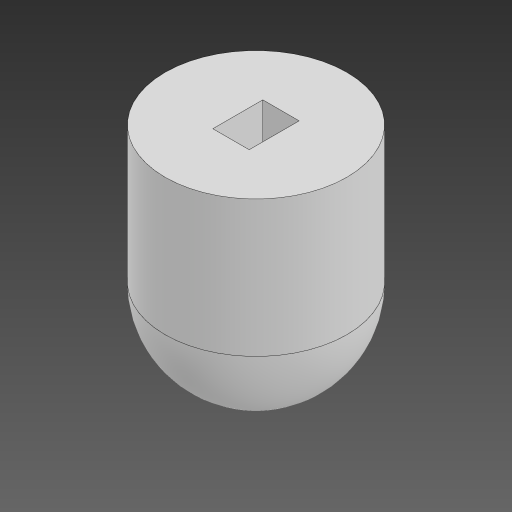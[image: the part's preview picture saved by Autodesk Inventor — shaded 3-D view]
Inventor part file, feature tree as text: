
AUTODESK INVENTOR PART (.ipt)
format: ipt  version: 2023.2 (Build 272271000, 271)  size: 117,248 bytes
history: native  units: mm
features: extrude x2, sketch x1, fillet x1
ambient origin geometry x8: Origin, YZ Plane, XZ Plane, XY Plane, X Axis, Y Axis, Z Axis, Center Point
bodies: Solid1 (feature_tree)
feature tree (4):
  sketch  "Sketch1"  dims[d0=1.6mm d1=2.2mm d2=8.0mm d3=10.0mm d4=0.0mm d5=5.0mm d6=0.0mm d7=4.0mm]
  extrude  "Extrusion1"  Depth=2.2mm
  extrude  "Extrusion2"  Depth=4.0mm
  fillet  "Fillet1"  Radius=10.0mm
